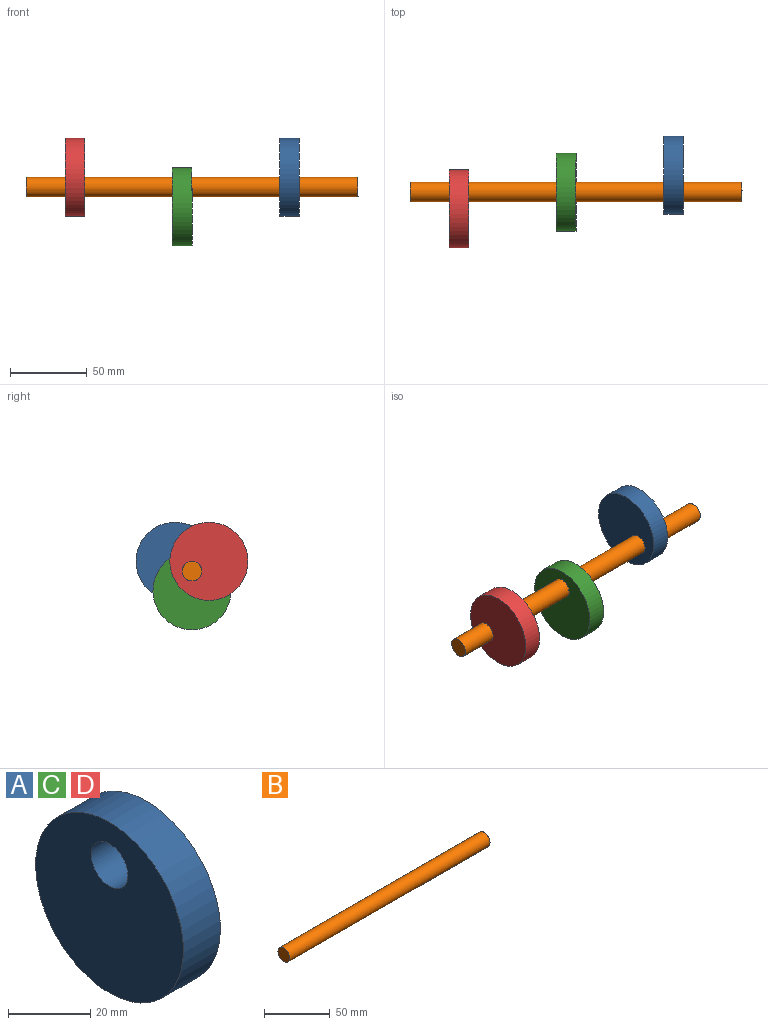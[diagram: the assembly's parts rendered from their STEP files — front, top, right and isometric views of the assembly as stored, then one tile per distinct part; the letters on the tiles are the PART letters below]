
ASSEMBLY  parts=4 mates=3
PART A: 4 faces, bbox 12.7x50.8x50.8 mm
  f0: plane 50.8x50.8mm, normal (1,0,0), area 1900.2mm2, adj f2,f3
  f1: plane 50.8x50.8mm, normal (-1,0,0), area 1900.2mm2, adj f2,f3
  f2: cylinder r=25.4mm len=50.8mm, axis (-1,0,0), area 2026.8mm2, adj f0,f1
  f3: cylinder r=6.35mm len=12.7mm, axis (-1,0,0), area 506.7mm2, adj f0,f1
PART B: 3 faces, bbox 215.9x12.7x12.7 mm
  f0: plane 12.7x12.7mm, normal (-1,0,0), area 126.7mm2, adj f2
  f1: plane 12.7x12.7mm, normal (1,0,0), area 126.7mm2, adj f2
  f2: cylinder r=6.35mm len=215.9mm, axis (-1,0,0), area 8614mm2, adj f0,f1
PART C: same geometry as A
PART D: same geometry as A
PLACE A rot(axis=(1,0,0),120deg) t=(45.38,96.83,132.99)mm
PLACE B rot(axis=(-1,0,0),120deg) t=(-94.32,-2.16,132.99)mm
PLACE C t=(-24.47,47.34,47.26)mm
PLACE D rot(axis=(-1,0,0),120deg) t=(-94.32,-2.16,132.99)mm
MATE fastened A.f3 <-> B.f2  axis (-1,0,0) through (-24.47,47.34,104.41)mm
MATE fastened C.f3 <-> B.f2  axis (-1,0,0) through (-94.32,47.34,104.41)mm
MATE fastened D.f3 <-> B.f2  axis (-1,0,0) through (-164.17,47.34,104.41)mm
